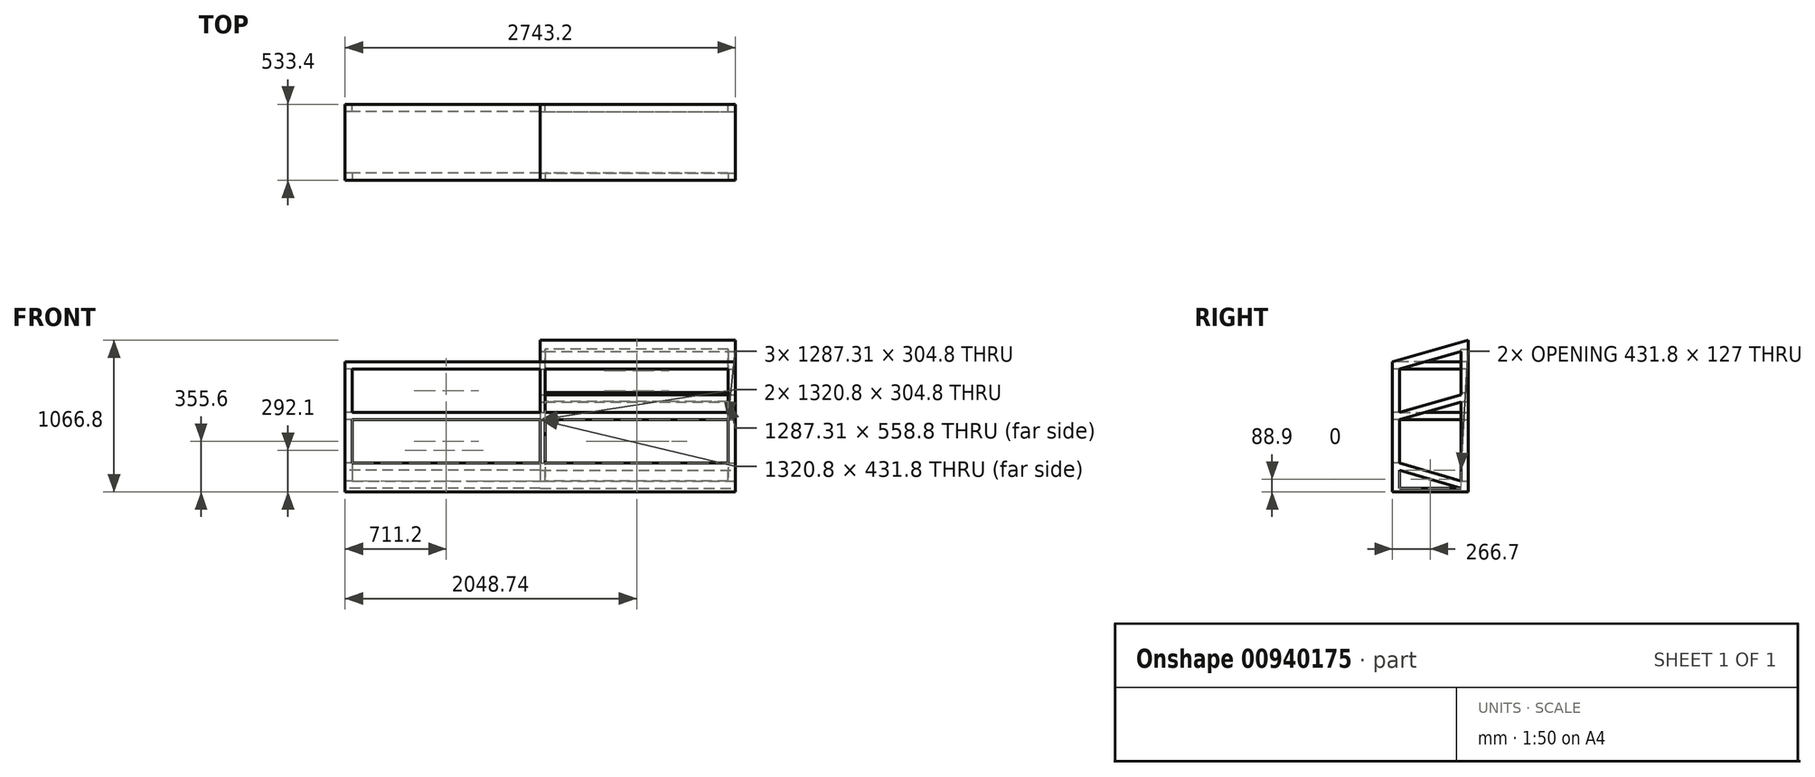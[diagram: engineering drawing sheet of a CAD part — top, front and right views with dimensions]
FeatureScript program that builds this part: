
annotation { "Feature Type Name" : "Feature", "Feature Type Description" : "" }
export const myFeature = defineFeature(function(context is Context, id is Id, definition is map)
    precondition{}
    {
        {
            var Q0;
            Q0=qCreatedBy(makeId("Top.planeOp"),FACE);
            var sketch = newSketch(context, id + "F0", { "sketchPlane" : qUnion([Q0])});
            skLineSegment(sketch, "E0.bottom", {"start": v(-1405.09, 73.8) * mm, "end": v(1338.11, 73.8) * mm});
            skLineSegment(sketch, "E0.top", {"start": v(-1405.09, -459.6) * mm, "end": v(1338.11, -459.6) * mm});
            skLineSegment(sketch, "E0.left", {"start": v(-1405.09, 73.8) * mm, "end": v(-1405.09, -459.6) * mm});
            skLineSegment(sketch, "E0.right", {"start": v(1338.11, 73.8) * mm, "end": v(1338.11, -459.6) * mm});
            skSolve(sketch);
        }
        {
            var Q0;
            Q0 = qSketchRegion(id + "F0", true);
            extrude(context, id + "F1", {"entities" : qUnion([Q0]), "depth" : 1066.8 * mm, "offsetDistance" : 25.4 * mm});
        }
        {
            var Q0;
            Q0=makeQuery(id+"F1.opExtrude","SWEPT_FACE",FACE,{"disambiguationData":[OSD([sQuery(id+"F0.wireOp",EDGE,"E0.right")])]});
            var sketch = newSketch(context, id + "F2", { "sketchPlane" : qUnion([Q0])});
            skLineSegment(sketch, "E1", {"start": v(-459.6, 1066.8) * mm, "end": v(-459.6, 914.4) * mm});
            skLineSegment(sketch, "E2", {"start": v(-459.6, 914.4) * mm, "end": v(73.8, 1066.8) * mm});
            skLineSegment(sketch, "E3", {"start": v(73.8, 1066.8) * mm, "end": v(-459.6, 1066.8) * mm});
            skSolve(sketch);
        }
        {
            var Q0;
            Q0 = qSketchRegion(id + "F2", true);
            extrude(context, id + "F3", {"entities" : qUnion([Q0]), "operationType" : NewBodyOperationType.REMOVE, "oppositeDirection" : true, "depth" : 1371.6 * mm, "offsetDistance" : 25.4 * mm});
        }
        {
            var Q0;
            Q0=makeQuery(id+"F1.opExtrude","SWEPT_FACE",FACE,{"disambiguationData":[OSD([sQuery(id+"F0.wireOp",EDGE,"E0.left")])]});
            var sketch = newSketch(context, id + "F4", { "sketchPlane" : qUnion([Q0])});
            skLineSegment(sketch, "E4.bottom", {"start": v(-73.8, 1066.8) * mm, "end": v(459.6, 1066.8) * mm});
            skLineSegment(sketch, "E4.top", {"start": v(-73.8, 914.4) * mm, "end": v(459.6, 914.4) * mm});
            skLineSegment(sketch, "E4.left", {"start": v(-73.8, 1066.8) * mm, "end": v(-73.8, 914.4) * mm});
            skLineSegment(sketch, "E4.right", {"start": v(459.6, 1066.8) * mm, "end": v(459.6, 914.4) * mm});
            skSolve(sketch);
        }
        {
            var Q0;
            Q0=makeQuery(id+"F4.imprint","IMPRINT",FACE,{"disambiguationData":[TD([[makeQuery(id+"F4.imprint","IMPRINT",EDGE,{"derivedFrom":sQuery(id+"F4.wireOp",EDGE,"E4.bottom")}),-1.0]])]});
            extrude(context, id + "F5", {"entities" : qUnion([Q0]), "operationType" : NewBodyOperationType.REMOVE, "oppositeDirection" : true, "depth" : 1371.6 * mm, "offsetDistance" : 25.4 * mm});
        }
        {
            var Q0;
            Q0=makeQuery(id+"F1.opExtrude","SWEPT_FACE",FACE,{"disambiguationData":[OSD([sQuery(id+"F0.wireOp",EDGE,"E0.right")])]});
            var sketch = newSketch(context, id + "F6", { "sketchPlane" : qUnion([Q0])});
            skLineSegment(sketch, "E5", {"start": v(-408.8, 863.6) * mm, "end": v(-408.8, 558.8) * mm});
            skLineSegment(sketch, "E6", {"start": v(-408.8, 558.8) * mm, "end": v(23, 682.17) * mm});
            skLineSegment(sketch, "E7", {"start": v(23, 682.17) * mm, "end": v(23, 986.97) * mm});
            skLineSegment(sketch, "E8", {"start": v(23, 986.97) * mm, "end": v(-408.8, 863.6) * mm});
            skLineSegment(sketch, "E9", {"start": v(23, 381) * mm, "end": v(23, 76.2) * mm});
            skLineSegment(sketch, "E10", {"start": v(23, 76.2) * mm, "end": v(-408.8, 203.2) * mm});
            skLineSegment(sketch, "E11", {"start": v(-408.8, 203.2) * mm, "end": v(-408.8, 508) * mm});
            skLineSegment(sketch, "E12", {"start": v(23, 631.37) * mm, "end": v(23, 431.8) * mm});
            skLineSegment(sketch, "E13", {"start": v(-537, 471.37) * mm, "end": v(23, 631.37) * mm});
            skLineSegment(sketch, "E14", {"start": v(-408.8, 152.4) * mm, "end": v(23, 25.4) * mm});
            skLineSegment(sketch, "E15", {"start": v(23, 25.4) * mm, "end": v(-408.8, 25.4) * mm});
            skLineSegment(sketch, "E16", {"start": v(-408.8, 25.4) * mm, "end": v(-408.8, 152.4) * mm});
            skLineSegment(sketch, "E17", {"start": v(-408.8, 508) * mm, "end": v(-537, 471.37) * mm});
            skLineSegment(sketch, "E18", {"start": v(23, 381) * mm, "end": v(23, 431.8) * mm});
            skSolve(sketch);
        }
        {
            var Q0;
            Q0=makeQuery(id+"F6.imprint","IMPRINT",FACE,{"disambiguationData":[TD([[makeQuery(id+"F6.imprint","IMPRINT",EDGE,{"derivedFrom":sQuery(id+"F6.wireOp",EDGE,"E5")}),1.0]])]});
            var Q1;
            Q1=makeQuery(id+"F6.imprint","IMPRINT",FACE,{"disambiguationData":[TD([[makeQuery(id+"F6.imprint","IMPRINT",EDGE,{"derivedFrom":sQuery(id+"F6.wireOp",EDGE,"E12")}),-1.0]])]});
            var Q2;
            Q2=makeQuery(id+"F6.imprint","IMPRINT",FACE,{"disambiguationData":[TD([[makeQuery(id+"F6.imprint","IMPRINT",EDGE,{"derivedFrom":sQuery(id+"F6.wireOp",EDGE,"cKYcgBJM-oVlt-VG9P-oxGC-OMHsgxLRpR4r")}),-1.0]])]});
            var Q3;
            Q3=makeQuery(id+"F6.imprint","IMPRINT",FACE,{"disambiguationData":[TD([[makeQuery(id+"F6.imprint","IMPRINT",EDGE,{"derivedFrom":sQuery(id+"F6.wireOp",EDGE,"E14")}),-1.0]])]});
            extrude(context, id + "F7", {"entities" : qUnion([Q0, Q1, Q2, Q3]), "operationType" : NewBodyOperationType.REMOVE, "oppositeDirection" : true, "depth" : 1371.6 * mm, "offsetDistance" : 25.4 * mm});
        }
        {
            var Q0;
            Q0=makeQuery(id+"F1.opExtrude","SWEPT_FACE",FACE,{"disambiguationData":[OSD([sQuery(id+"F0.wireOp",EDGE,"E0.top")])]});
            var sketch = newSketch(context, id + "F8", { "sketchPlane" : qUnion([Q0])});
            skLineSegment(sketch, "E19.bottom", {"start": v(0, 863.6) * mm, "end": v(1287.31, 863.6) * mm});
            skLineSegment(sketch, "E19.top", {"start": v(0, 558.8) * mm, "end": v(1287.31, 558.8) * mm});
            skLineSegment(sketch, "E19.left", {"start": v(0, 863.6) * mm, "end": v(0, 558.8) * mm});
            skLineSegment(sketch, "E19.right", {"start": v(1287.31, 863.6) * mm, "end": v(1287.31, 558.8) * mm});
            skSolve(sketch);
        }
        {
            var Q0;
            Q0=makeQuery(id+"F8.imprint","IMPRINT",FACE,{"disambiguationData":[TD([[makeQuery(id+"F8.imprint","IMPRINT",EDGE,{"derivedFrom":sQuery(id+"F8.wireOp",EDGE,"E19.bottom")}),-1.0]])]});
            var Q1;
            Q1=makeQuery(id+"F7.boolean.opBoolean","COPY",FACE,{"derivedFrom":makeQuery(id+"F7.opExtrude","SWEPT_FACE",FACE,{"disambiguationData":[OSD([sQuery(id+"F6.wireOp",EDGE,"E5")])]})});
            extrude(context, id + "F9", {"entities" : qUnion([Q0]), "operationType" : NewBodyOperationType.REMOVE, "endBound" : BoundingType.UP_TO_SURFACE, "oppositeDirection" : true, "depth" : 25.4 * mm, "endBoundEntityFace" : qUnion([Q1]), "offsetDistance" : 25.4 * mm});
        }
        {
            var Q0;
            Q0=makeQuery(id+"F1.opExtrude","SWEPT_FACE",FACE,{"disambiguationData":[OSD([sQuery(id+"F0.wireOp",EDGE,"E0.top")])]});
            var sketch = newSketch(context, id + "F10", { "sketchPlane" : qUnion([Q0])});
            skLineSegment(sketch, "E20", {"start": v(0, 508) * mm, "end": v(1287.31, 508) * mm});
            skLineSegment(sketch, "E21", {"start": v(1287.31, 508) * mm, "end": v(1287.31, 203.2) * mm});
            skLineSegment(sketch, "E22", {"start": v(1287.31, 203.2) * mm, "end": v(0, 203.2) * mm});
            skLineSegment(sketch, "E23", {"start": v(0, 203.2) * mm, "end": v(0, 508) * mm});
            skSolve(sketch);
        }
        {
            var Q0;
            Q0 = qSketchRegion(id + "F10", true);
            var Q1;
            Q1=makeQuery(id+"F7.boolean.opBoolean","COPY",FACE,{"derivedFrom":makeQuery(id+"F7.opExtrude","SWEPT_FACE",FACE,{"disambiguationData":[OSD([sQuery(id+"F6.wireOp",EDGE,"E11")])]})});
            extrude(context, id + "F11", {"entities" : qUnion([Q0]), "operationType" : NewBodyOperationType.REMOVE, "endBound" : BoundingType.UP_TO_SURFACE, "oppositeDirection" : true, "depth" : 25.4 * mm, "endBoundEntityFace" : qUnion([Q1]), "offsetDistance" : 25.4 * mm});
        }
        {
            var Q0;
            Q0=makeQuery(id+"F1.opExtrude","SWEPT_FACE",FACE,{"disambiguationData":[OSD([sQuery(id+"F0.wireOp",EDGE,"E0.bottom")])]});
            var sketch = newSketch(context, id + "F12", { "sketchPlane" : qUnion([Q0])});
            skLineSegment(sketch, "E24.bottom", {"start": v(-1287.31, 1003.3) * mm, "end": v(0, 1003.3) * mm});
            skLineSegment(sketch, "E24.top", {"start": v(-1287.31, 698.5) * mm, "end": v(0, 698.5) * mm});
            skLineSegment(sketch, "E24.left", {"start": v(-1287.31, 1003.3) * mm, "end": v(-1287.31, 698.5) * mm});
            skLineSegment(sketch, "E24.right", {"start": v(0, 1003.3) * mm, "end": v(0, 698.5) * mm});
            skLineSegment(sketch, "E25.top", {"start": v(-1287.31, 76.2) * mm, "end": v(0, 76.2) * mm});
            skLineSegment(sketch, "E25.left", {"start": v(-1287.31, 393.7) * mm, "end": v(-1287.31, 76.2) * mm});
            skLineSegment(sketch, "E25.right", {"start": v(0, 393.7) * mm, "end": v(0, 76.2) * mm});
            skLineSegment(sketch, "E26.bottom", {"start": v(-1287.31, 635) * mm, "end": v(0, 635) * mm});
            skLineSegment(sketch, "E26.left", {"start": v(-1287.31, 635) * mm, "end": v(-1287.31, 444.5) * mm});
            skLineSegment(sketch, "E26.right", {"start": v(0, 635) * mm, "end": v(0, 444.5) * mm});
            skLineSegment(sketch, "E27", {"start": v(-1287.31, 444.5) * mm, "end": v(-1287.31, 393.7) * mm});
            skLineSegment(sketch, "E28", {"start": v(0, 444.5) * mm, "end": v(0, 393.7) * mm});
            skSolve(sketch);
        }
        {
            var Q0;
            Q0 = qSketchRegion(id + "F12", true);
            var Q1;
            Q1=makeQuery(id+"F7.boolean.opBoolean","COPY",FACE,{"derivedFrom":makeQuery(id+"F7.opExtrude","SWEPT_FACE",FACE,{"disambiguationData":[OSD([sQuery(id+"F6.wireOp",EDGE,"E7")])]})});
            extrude(context, id + "F13", {"entities" : qUnion([Q0]), "operationType" : NewBodyOperationType.REMOVE, "endBound" : BoundingType.UP_TO_SURFACE, "oppositeDirection" : true, "depth" : 25.4 * mm, "endBoundEntityFace" : qUnion([Q1]), "offsetDistance" : 25.4 * mm});
        }
        {
            var Q0;
            Q0=makeQuery(id+"F1.opExtrude","SWEPT_FACE",FACE,{"disambiguationData":[OSD([sQuery(id+"F0.wireOp",EDGE,"E0.left")])]});
            var sketch = newSketch(context, id + "F14", { "sketchPlane" : qUnion([Q0])});
            skLineSegment(sketch, "E29", {"start": v(408.8, 863.6) * mm, "end": v(408.8, 558.8) * mm});
            skLineSegment(sketch, "E30", {"start": v(408.8, 558.8) * mm, "end": v(-302.4, 558.8) * mm});
            skLineSegment(sketch, "E31", {"start": v(-302.4, 558.8) * mm, "end": v(-302.4, 863.6) * mm});
            skLineSegment(sketch, "E32", {"start": v(-302.4, 863.6) * mm, "end": v(408.8, 863.6) * mm});
            skSolve(sketch);
        }
        {
            var Q0;
            Q0 = qSketchRegion(id + "F14", true);
            extrude(context, id + "F15", {"entities" : qUnion([Q0]), "operationType" : NewBodyOperationType.REMOVE, "oppositeDirection" : true, "depth" : 1371.6 * mm, "offsetDistance" : 25.4 * mm});
        }
        {
            var Q0;
            Q0=makeQuery(id+"F1.opExtrude","SWEPT_FACE",FACE,{"disambiguationData":[OSD([sQuery(id+"F0.wireOp",EDGE,"E0.left")])]});
            var sketch = newSketch(context, id + "F16", { "sketchPlane" : qUnion([Q0])});
            skLineSegment(sketch, "E33", {"start": v(408.8, 442.92) * mm, "end": v(408.8, 203.2) * mm});
            skLineSegment(sketch, "E34", {"start": v(408.8, 203.2) * mm, "end": v(-23, 76.2) * mm});
            skLineSegment(sketch, "E35", {"start": v(-23, 76.2) * mm, "end": v(-23, 355.6) * mm});
            skLineSegment(sketch, "E36", {"start": v(-23, 508) * mm, "end": v(408.8, 508) * mm});
            skLineSegment(sketch, "E37", {"start": v(408.8, 508) * mm, "end": v(408.8, 493.72) * mm});
            skLineSegment(sketch, "E38", {"start": v(-23, 406.4) * mm, "end": v(-23, 508) * mm});
            skLineSegment(sketch, "E39", {"start": v(-23, 406.4) * mm, "end": v(-23, 355.6) * mm});
            skLineSegment(sketch, "E40", {"start": v(408.8, 493.72) * mm, "end": v(408.8, 442.92) * mm});
            skLineSegment(sketch, "E41", {"start": v(408.8, 25.4) * mm, "end": v(408.8, 152.4) * mm});
            skLineSegment(sketch, "E42", {"start": v(408.8, 152.4) * mm, "end": v(-23, 25.4) * mm});
            skLineSegment(sketch, "E43", {"start": v(-23, 25.4) * mm, "end": v(408.8, 25.4) * mm});
            skSolve(sketch);
        }
        {
            var Q0;
            Q0 = qSketchRegion(id + "F16", true);
            extrude(context, id + "F17", {"entities" : qUnion([Q0]), "operationType" : NewBodyOperationType.REMOVE, "oppositeDirection" : true, "depth" : 1371.6 * mm, "offsetDistance" : 25.4 * mm});
        }
        {
            var Q0;
            Q0=makeQuery(id+"F1.opExtrude","SWEPT_FACE",FACE,{"disambiguationData":[OSD([sQuery(id+"F0.wireOp",EDGE,"E0.bottom")])]});
            var sketch = newSketch(context, id + "F18", { "sketchPlane" : qUnion([Q0])});
            skLineSegment(sketch, "E44.bottom", {"start": v(1354.29, 863.6) * mm, "end": v(33.49, 863.6) * mm});
            skLineSegment(sketch, "E44.top", {"start": v(1354.29, 558.8) * mm, "end": v(33.49, 558.8) * mm});
            skLineSegment(sketch, "E44.left", {"start": v(1354.29, 863.6) * mm, "end": v(1354.29, 558.8) * mm});
            skLineSegment(sketch, "E44.right", {"start": v(33.49, 863.6) * mm, "end": v(33.49, 558.8) * mm});
            skLineSegment(sketch, "E45.top", {"start": v(1354.29, 76.2) * mm, "end": v(33.49, 76.2) * mm});
            skLineSegment(sketch, "E45.left", {"start": v(1354.29, 355.6) * mm, "end": v(1354.29, 76.2) * mm});
            skLineSegment(sketch, "E45.right", {"start": v(33.49, 355.6) * mm, "end": v(33.49, 76.2) * mm});
            skLineSegment(sketch, "E46.bottom", {"start": v(33.49, 508) * mm, "end": v(1354.29, 508) * mm});
            skLineSegment(sketch, "E46.left", {"start": v(33.49, 508) * mm, "end": v(33.49, 406.4) * mm});
            skLineSegment(sketch, "E46.right", {"start": v(1354.29, 508) * mm, "end": v(1354.29, 406.4) * mm});
            skLineSegment(sketch, "E47", {"start": v(1354.29, 406.4) * mm, "end": v(1354.29, 355.6) * mm});
            skLineSegment(sketch, "E48", {"start": v(33.49, 406.4) * mm, "end": v(33.49, 355.6) * mm});
            skSolve(sketch);
        }
        {
            var Q0;
            Q0 = qSketchRegion(id + "F18", true);
            var Q1;
            Q1=makeQuery(id+"F17.boolean.opBoolean","MERGE",FACE,{"derivedFrom":[makeQuery(id+"F15.boolean.opBoolean","MERGE",FACE,{"derivedFrom":[makeQuery(id+"F7.boolean.opBoolean","COPY",FACE,{"derivedFrom":makeQuery(id+"F7.opExtrude","SWEPT_FACE",FACE,{"disambiguationData":[OSD([sQuery(id+"F6.wireOp",EDGE,"E7")])]})}),makeQuery(id+"F7.boolean.opBoolean","COPY",FACE,{"derivedFrom":makeQuery(id+"F7.opExtrude","SWEPT_FACE",FACE,{"disambiguationData":[OSD([sQuery(id+"F6.wireOp",EDGE,"E12")])]})})],"fromTools":[makeQuery(id+"F15.opExtrude","SWEPT_FACE",FACE,{"disambiguationData":[OSD([sQuery(id+"F14.wireOp",EDGE,"E31")])]})]})],"fromTools":[makeQuery(id+"F17.opExtrude","SWEPT_FACE",FACE,{"disambiguationData":[OSD([sQuery(id+"F16.wireOp",EDGE,"E38")])]})]});
            extrude(context, id + "F19", {"entities" : qUnion([Q0]), "operationType" : NewBodyOperationType.REMOVE, "endBound" : BoundingType.UP_TO_SURFACE, "oppositeDirection" : true, "depth" : 25.4 * mm, "endBoundEntityFace" : qUnion([Q1]), "offsetDistance" : 25.4 * mm});
        }
        {
            var Q0;
            Q0=makeQuery(id+"F1.opExtrude","SWEPT_FACE",FACE,{"disambiguationData":[OSD([sQuery(id+"F0.wireOp",EDGE,"E0.top")])]});
            var sketch = newSketch(context, id + "F20", { "sketchPlane" : qUnion([Q0])});
            skLineSegment(sketch, "E49.bottom", {"start": v(-33.49, 863.6) * mm, "end": v(-1354.29, 863.6) * mm});
            skLineSegment(sketch, "E49.top", {"start": v(-33.49, 558.8) * mm, "end": v(-1354.29, 558.8) * mm});
            skLineSegment(sketch, "E49.left", {"start": v(-33.49, 863.6) * mm, "end": v(-33.49, 558.8) * mm});
            skLineSegment(sketch, "E49.right", {"start": v(-1354.29, 863.6) * mm, "end": v(-1354.29, 558.8) * mm});
            skLineSegment(sketch, "E50.bottom", {"start": v(-1354.29, 508) * mm, "end": v(-33.49, 508) * mm});
            skLineSegment(sketch, "E50.top", {"start": v(-1354.29, 203.2) * mm, "end": v(-33.49, 203.2) * mm});
            skLineSegment(sketch, "E50.left", {"start": v(-1354.29, 508) * mm, "end": v(-1354.29, 203.2) * mm});
            skLineSegment(sketch, "E50.right", {"start": v(-33.49, 508) * mm, "end": v(-33.49, 203.2) * mm});
            skSolve(sketch);
        }
        {
            var Q0;
            Q0 = qSketchRegion(id + "F20", true);
            var Q1;
            {var subQ2=sQuery(id+"F6.wireOp",EDGE,"E5");Q1=makeQuery(id+"F15.boolean.opBoolean","MERGE",FACE,{"derivedFrom":[makeQuery(id+"F9.boolean.opBoolean","SPLIT",FACE,{"disambiguationData":[TD([makeQuery(id+"F9.opExtrude","SWEPT_FACE",FACE,{"disambiguationData":[OSD([sQuery(id+"F8.wireOp",EDGE,"E19.left")])]})])],"derivedFrom":makeQuery(id+"F7.boolean.opBoolean","COPY",FACE,{"derivedFrom":makeQuery(id+"F7.opExtrude","SWEPT_FACE",FACE,{"disambiguationData":[OSD([subQ2])]})})})],"fromTools":[makeQuery(id+"F15.opExtrude","SWEPT_FACE",FACE,{"disambiguationData":[OSD([sQuery(id+"F14.wireOp",EDGE,"E29")])]})]});}
            extrude(context, id + "F21", {"entities" : qUnion([Q0]), "operationType" : NewBodyOperationType.REMOVE, "endBound" : BoundingType.UP_TO_SURFACE, "oppositeDirection" : true, "depth" : 25.4 * mm, "endBoundEntityFace" : qUnion([Q1]), "offsetDistance" : 25.4 * mm});
        }
    });
